# Revit family: FantiniCosmi_BIM_B71A
name_source: partatom
category: Generic Models
units: mm (PartAtom-declared; Revit-internal decimal feet)

## family parameters
Always vertical = Yes
Can host rebar = No
Cut with Voids When Loaded = No
Part Type = Normal
Room Calculation Point = No
Round Connector Dimension = Use Diameter
Shared = No
Work Plane-Based = No

## types (1)
- Standard
    Catalog web link = https://www.fantinicosmi.it
    Connection = biphase
    Connection G 1/4 = Female
    Default Elevation = 0 mm  [stored 0 ft]
    Description = Pressure switches for single-phase / two-phase motors direct control
    Designer = Carniti
    Differential (Full scale) = 1.2 ÷ 2.3 bar
    Differential (Start of scale) = 1.0 ÷ 2.1 bar
    Maximum differential = 2.3 bar
    Maximum temperature of the controlled fluid = 70°C
    PROTECTION DEGREE = IP20
    Part Number = B71A
    Pressure switch body admissible temperature = -15 ÷ 60°C
    Range = 1.5 ÷ 4.5 bar
    Storage and transport temperature = -15 ÷ 60°C
    Weight = 0,35 Kg

note: [stored X ft] marks values corroborated as IEEE doubles in the binary element streams (Revit-internal decimal feet)

## geometry (parser evidence)
native form markers: Sweep x3
no freeform markers — native parametric forms only
